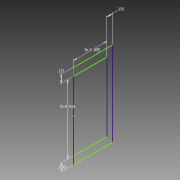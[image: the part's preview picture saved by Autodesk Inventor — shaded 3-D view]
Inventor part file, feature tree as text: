
AUTODESK INVENTOR PART (.ipt)
format: ipt  version: 2014 (Build 180170000, 170)  size: 67,584 bytes
history: native  units: in
note: dims shown in document units (in); Inventor stores cm internally (conversion verified against a paired STEP export)
features: sketch x1
ambient origin geometry x8: Origin, YZ Plane, XZ Plane, XY Plane, X Axis, Y Axis, Z Axis, Center Point
feature tree (1):
  sketch  "Sketch1"  dims[d2=2.1654in d3=0.5in d4=0.5in d5=0.375in d6=4.5157in]
